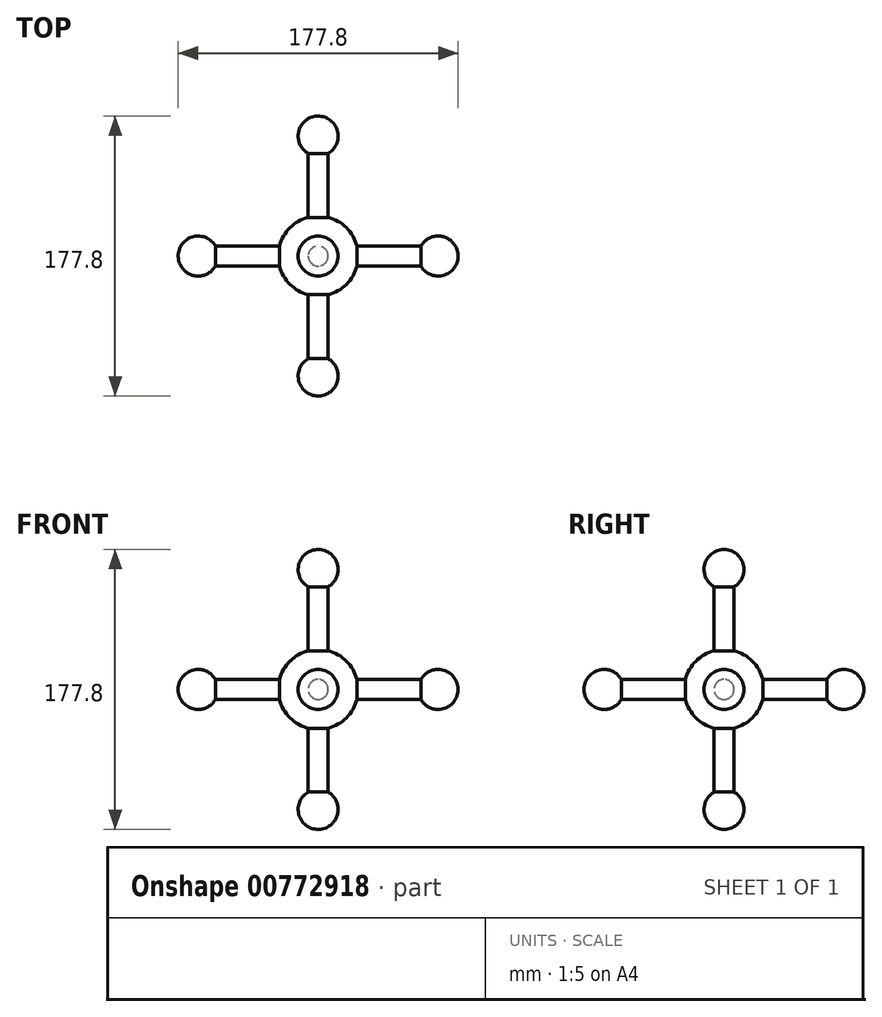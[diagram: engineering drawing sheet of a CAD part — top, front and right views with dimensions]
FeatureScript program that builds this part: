
annotation { "Feature Type Name" : "Feature", "Feature Type Description" : "" }
export const myFeature = defineFeature(function(context is Context, id is Id, definition is map)
    precondition{}
    {
        {
            var Q0;
            Q0=qCreatedBy(makeId("Front.planeOp"),FACE);
            var sketch = newSketch(context, id + "F0", { "sketchPlane" : qUnion([Q0])});
            skLineSegment(sketch, "E0", {"start": v(0, 0) * mm, "end": v(0, 25.4) * mm});
            skLineSegment(sketch, "E1", {"start": v(0, 0) * mm, "end": v(0, -25.4) * mm});
            skArc(sketch, "E2", {"start": v(0, -25.4) * mm, "mid": v(25.4, 0) * mm, "end": v(0, 25.4) * mm});
            skSolve(sketch);
        }
        {
            var Q0;
            Q0 = qSketchRegion(id + "F0", true);
            var Q1;
            Q1=sQuery(id+"F0.wireOp",EDGE,"E0");
            revolve(context, id + "F1", {"surfaceOperationType" : NewSurfaceOperationType.NEW, "entities" : qUnion([Q0]), "axis" : qUnion([Q1]), "revolveType" : RevolveType.FULL});
        }
        {
            var Q0;
            Q0=qCreatedBy(makeId("Right.planeOp"),FACE);
            var sketch = newSketch(context, id + "F2", { "sketchPlane" : qUnion([Q0])});
            skCircle(sketch, "E3", {"center": v(0, 0) * mm, "radius": 6.35 * mm});
            skSolve(sketch);
        }
        {
            var Q0;
            Q0 = qSketchRegion(id + "F2", true);
            extrude(context, id + "F3", {"entities" : qUnion([Q0]), "operationType" : NewBodyOperationType.ADD, "depth" : 76.2 * mm, "offsetDistance" : 25.4 * mm});
        }
        {
            var Q0;
            Q0 = qSketchRegion(id + "F2", true);
            extrude(context, id + "F4", {"entities" : qUnion([Q0]), "operationType" : NewBodyOperationType.ADD, "oppositeDirection" : true, "depth" : 76.2 * mm, "offsetDistance" : 25.4 * mm});
        }
        {
            var Q0;
            Q0=qCreatedBy(makeId("Top.planeOp"),FACE);
            var sketch = newSketch(context, id + "F5", { "sketchPlane" : qUnion([Q0])});
            skCircle(sketch, "E4", {"center": v(0, 0) * mm, "radius": 6.35 * mm});
            skSolve(sketch);
        }
        {
            var Q0;
            Q0 = qSketchRegion(id + "F5", true);
            extrude(context, id + "F6", {"entities" : qUnion([Q0]), "operationType" : NewBodyOperationType.ADD, "depth" : 76.2 * mm, "offsetDistance" : 25.4 * mm});
        }
        {
            var Q0;
            Q0 = qSketchRegion(id + "F5", true);
            extrude(context, id + "F7", {"entities" : qUnion([Q0]), "operationType" : NewBodyOperationType.ADD, "oppositeDirection" : true, "depth" : 76.2 * mm, "offsetDistance" : 25.4 * mm});
        }
        {
            var Q0;
            Q0=qCreatedBy(makeId("Front.planeOp"),FACE);
            var sketch = newSketch(context, id + "F8", { "sketchPlane" : qUnion([Q0])});
            skCircle(sketch, "E5", {"center": v(0, 0) * mm, "radius": 6.35 * mm});
            skSolve(sketch);
        }
        {
            var Q0;
            Q0 = qSketchRegion(id + "F8", true);
            extrude(context, id + "F9", {"entities" : qUnion([Q0]), "operationType" : NewBodyOperationType.ADD, "depth" : 76.2 * mm, "offsetDistance" : 25.4 * mm});
        }
        {
            var Q0;
            Q0 = qSketchRegion(id + "F8", true);
            extrude(context, id + "F10", {"entities" : qUnion([Q0]), "operationType" : NewBodyOperationType.ADD, "oppositeDirection" : true, "depth" : 76.2 * mm, "offsetDistance" : 25.4 * mm});
        }
        {
            var Q0;
            Q0=makeQuery(id+"F6.opExtrude","CAP_FACE",FACE,{"disambiguationData":[OSD([sQuery(id+"F5.wireOp",EDGE,"E4")])],"isStart":false});
            var sketch = newSketch(context, id + "F11", { "sketchPlane" : qUnion([Q0])});
            skLineSegment(sketch, "E6", {"start": v(0, 0) * mm, "end": v(0, 12.7) * mm});
            skLineSegment(sketch, "E7", {"start": v(0, 0) * mm, "end": v(0, -12.7) * mm});
            skArc(sketch, "E8", {"start": v(0, -12.7) * mm, "mid": v(12.7, 0) * mm, "end": v(0, 12.7) * mm});
            skSolve(sketch);
        }
        {
            var Q0;
            Q0 = qSketchRegion(id + "F11", true);
            var Q1;
            Q1=sQuery(id+"F11.wireOp",EDGE,"E6");
            revolve(context, id + "F12", {"operationType" : NewBodyOperationType.ADD, "surfaceOperationType" : NewSurfaceOperationType.NEW, "entities" : qUnion([Q0]), "axis" : qUnion([Q1]), "revolveType" : RevolveType.FULL});
        }
        {
            var Q0;
            Q0=makeQuery(id+"F3.opExtrude","CAP_FACE",FACE,{"disambiguationData":[OSD([sQuery(id+"F2.wireOp",EDGE,"E3")])],"isStart":false});
            var sketch = newSketch(context, id + "F13", { "sketchPlane" : qUnion([Q0])});
            skLineSegment(sketch, "E9", {"start": v(0, 0) * mm, "end": v(0, 12.7) * mm});
            skLineSegment(sketch, "E10", {"start": v(0, 0) * mm, "end": v(0, -12.7) * mm});
            skArc(sketch, "E11", {"start": v(0, -12.7) * mm, "mid": v(12.7, 0) * mm, "end": v(0, 12.7) * mm});
            skSolve(sketch);
        }
        {
            var Q0;
            Q0 = qSketchRegion(id + "F13", true);
            var Q1;
            Q1=sQuery(id+"F13.wireOp",EDGE,"E9");
            revolve(context, id + "F14", {"operationType" : NewBodyOperationType.ADD, "surfaceOperationType" : NewSurfaceOperationType.NEW, "entities" : qUnion([Q0]), "axis" : qUnion([Q1]), "revolveType" : RevolveType.FULL});
        }
        {
            var Q0;
            Q0=makeQuery(id+"F4.opExtrude","CAP_FACE",FACE,{"disambiguationData":[OSD([sQuery(id+"F2.wireOp",EDGE,"E3")])],"isStart":false});
            var sketch = newSketch(context, id + "F15", { "sketchPlane" : qUnion([Q0])});
            skLineSegment(sketch, "E12", {"start": v(0, 0) * mm, "end": v(0, 12.7) * mm});
            skLineSegment(sketch, "E13", {"start": v(0, 0) * mm, "end": v(0, -12.7) * mm});
            skArc(sketch, "E14", {"start": v(0, -12.7) * mm, "mid": v(12.7, 0) * mm, "end": v(0, 12.7) * mm});
            skSolve(sketch);
        }
        {
            var Q0;
            Q0 = qSketchRegion(id + "F15", true);
            var Q1;
            Q1=sQuery(id+"F15.wireOp",EDGE,"E12");
            revolve(context, id + "F16", {"operationType" : NewBodyOperationType.ADD, "surfaceOperationType" : NewSurfaceOperationType.NEW, "entities" : qUnion([Q0]), "axis" : qUnion([Q1]), "revolveType" : RevolveType.FULL});
        }
        {
            var Q0;
            Q0=makeQuery(id+"F7.opExtrude","CAP_FACE",FACE,{"disambiguationData":[OSD([sQuery(id+"F5.wireOp",EDGE,"E4")])],"isStart":false});
            var sketch = newSketch(context, id + "F17", { "sketchPlane" : qUnion([Q0])});
            skLineSegment(sketch, "E15", {"start": v(0, 0) * mm, "end": v(0, 12.7) * mm});
            skLineSegment(sketch, "E16", {"start": v(0, 0) * mm, "end": v(0, -12.7) * mm});
            skArc(sketch, "E17", {"start": v(0, -12.7) * mm, "mid": v(12.7, 0) * mm, "end": v(0, 12.7) * mm});
            skSolve(sketch);
        }
        {
            var Q0;
            Q0 = qSketchRegion(id + "F17", true);
            var Q1;
            Q1=sQuery(id+"F17.wireOp",EDGE,"E15");
            revolve(context, id + "F18", {"operationType" : NewBodyOperationType.ADD, "surfaceOperationType" : NewSurfaceOperationType.NEW, "entities" : qUnion([Q0]), "axis" : qUnion([Q1]), "revolveType" : RevolveType.FULL});
        }
        {
            var Q0;
            Q0=makeQuery(id+"F9.opExtrude","CAP_FACE",FACE,{"disambiguationData":[OSD([sQuery(id+"F8.wireOp",EDGE,"E5")])],"isStart":false});
            var sketch = newSketch(context, id + "F19", { "sketchPlane" : qUnion([Q0])});
            skLineSegment(sketch, "E18", {"start": v(0, 0) * mm, "end": v(0, 12.7) * mm});
            skLineSegment(sketch, "E19", {"start": v(0, 0) * mm, "end": v(0, -12.7) * mm});
            skArc(sketch, "E20", {"start": v(0, -12.7) * mm, "mid": v(12.7, 0) * mm, "end": v(0, 12.7) * mm});
            skSolve(sketch);
        }
        {
            var Q0;
            Q0 = qSketchRegion(id + "F19", true);
            var Q1;
            Q1=sQuery(id+"F19.wireOp",EDGE,"E18");
            revolve(context, id + "F20", {"operationType" : NewBodyOperationType.ADD, "surfaceOperationType" : NewSurfaceOperationType.NEW, "entities" : qUnion([Q0]), "axis" : qUnion([Q1]), "revolveType" : RevolveType.FULL});
        }
        {
            var Q0;
            Q0=makeQuery(id+"F10.opExtrude","CAP_FACE",FACE,{"disambiguationData":[OSD([sQuery(id+"F8.wireOp",EDGE,"E5")])],"isStart":false});
            var sketch = newSketch(context, id + "F21", { "sketchPlane" : qUnion([Q0])});
            skLineSegment(sketch, "E21", {"start": v(0, 0) * mm, "end": v(0, 12.7) * mm});
            skLineSegment(sketch, "E22", {"start": v(0, 0) * mm, "end": v(0, -12.7) * mm});
            skArc(sketch, "E23", {"start": v(0, -12.7) * mm, "mid": v(12.7, 0) * mm, "end": v(0, 12.7) * mm});
            skSolve(sketch);
        }
        {
            var Q0;
            Q0 = qSketchRegion(id + "F21", true);
            var Q1;
            Q1=sQuery(id+"F21.wireOp",EDGE,"E21");
            revolve(context, id + "F22", {"operationType" : NewBodyOperationType.ADD, "surfaceOperationType" : NewSurfaceOperationType.NEW, "entities" : qUnion([Q0]), "axis" : qUnion([Q1]), "revolveType" : RevolveType.FULL});
        }
    });
